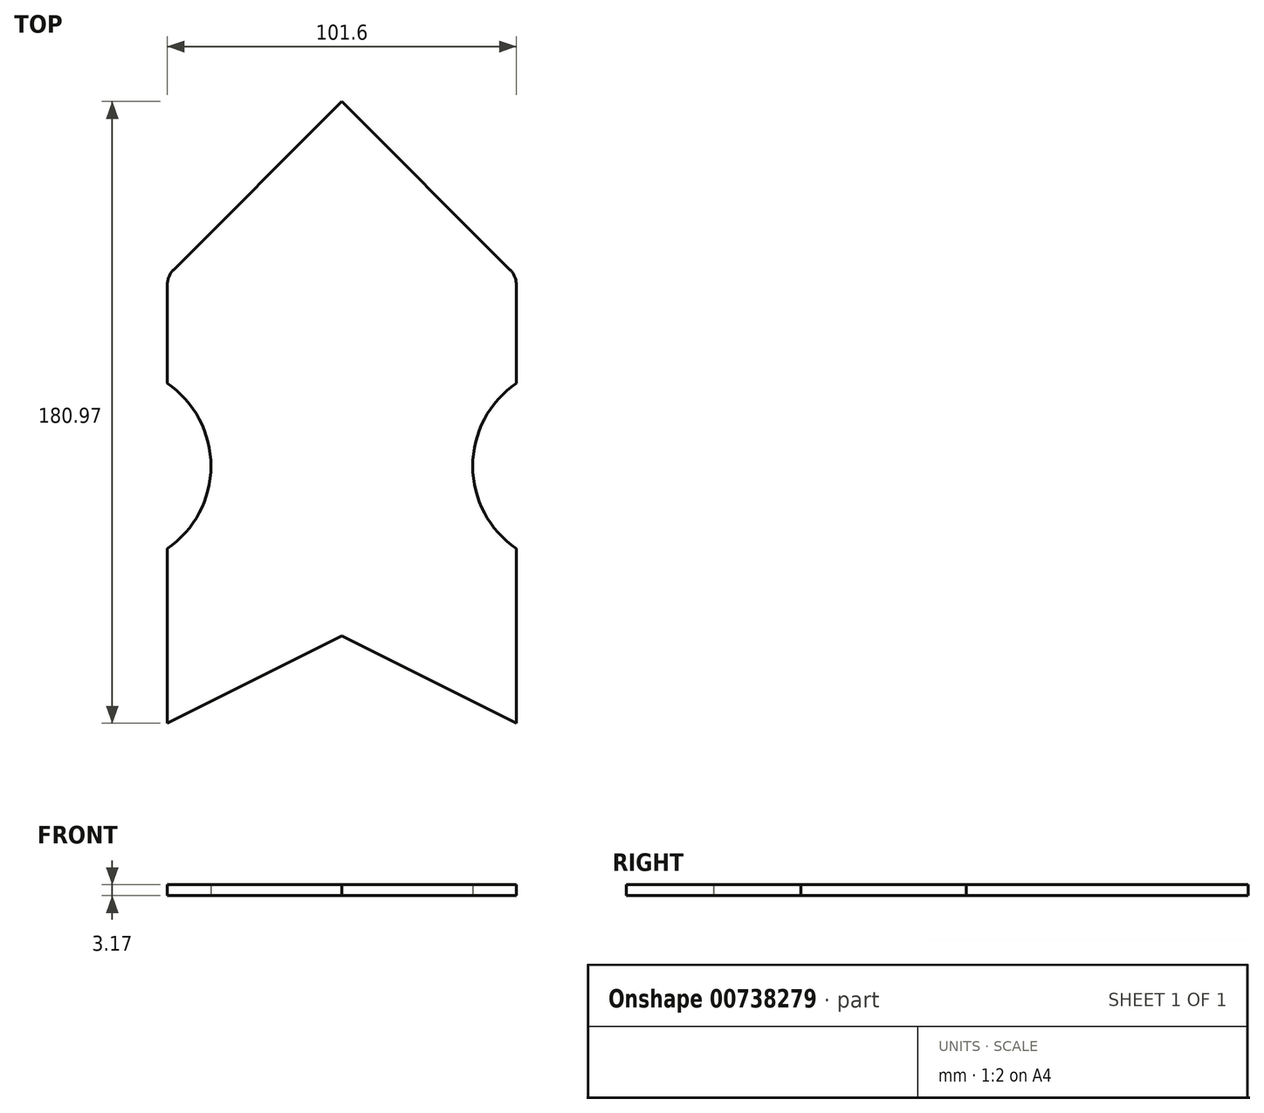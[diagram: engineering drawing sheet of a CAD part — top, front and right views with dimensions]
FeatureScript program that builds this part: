
annotation { "Feature Type Name" : "Feature", "Feature Type Description" : "" }
export const myFeature = defineFeature(function(context is Context, id is Id, definition is map)
    precondition{}
    {
        {
            var Q0;
            Q0=qCreatedBy(makeId("Top.planeOp"),FACE);
            var sketch = newSketch(context, id + "F0", { "sketchPlane" : qUnion([Q0])});
            skLineSegment(sketch, "E0", {"start": v(54.35, -30.5) * mm, "end": v(3.55, -5.1) * mm});
            skLineSegment(sketch, "E1", {"start": v(3.55, -5.1) * mm, "end": v(-47.25, -30.5) * mm});
            skLineSegment(sketch, "E2", {"start": v(-47.25, -30.5) * mm, "end": v(-47.25, 20.3) * mm});
            skLineSegment(sketch, "E3", {"start": v(54.35, -30.5) * mm, "end": v(54.35, 20.3) * mm});
            skLineSegment(sketch, "E4", {"start": v(54.35, 99.68) * mm, "end": v(-47.25, 99.68) * mm});
            skLineSegment(sketch, "E5", {"start": v(3.55, -5.1) * mm, "end": v(3.55, 150.48) * mm, "construction": true});
            skLineSegment(sketch, "E6", {"start": v(3.55, 150.48) * mm, "end": v(-45.39, 101.54) * mm});
            skLineSegment(sketch, "E7", {"start": v(52.5, 101.54) * mm, "end": v(3.55, 150.48) * mm});
            skLineSegment(sketch, "E8", {"start": v(-47.25, -30.5) * mm, "end": v(54.35, -30.5) * mm, "construction": true});
            skPoint(sketch, "E9.visualSharp", {"position": v(-47.25, 99.68) * mm});
            skArc(sketch, "E9.filletArc", {"start": v(-45.39, 101.54) * mm, "mid": v(-46.76, 99.48) * mm, "end": v(-47.25, 97.05) * mm});
            skPoint(sketch, "E10.visualSharp", {"position": v(54.35, 99.68) * mm});
            skArc(sketch, "E10.filletArc", {"start": v(54.35, 97.05) * mm, "mid": v(53.87, 99.48) * mm, "end": v(52.5, 101.54) * mm});
            skPoint(sketch, "E11", {"position": v(-47.25, 68.48) * mm});
            skPoint(sketch, "E12", {"position": v(-47.25, 20.3) * mm});
            skArc(sketch, "E13", {"start": v(-47.25, 20.3) * mm, "mid": v(-34.55, 44.4) * mm, "end": v(-47.25, 68.48) * mm});
            skPoint(sketch, "E14", {"position": v(54.35, 68.48) * mm});
            skPoint(sketch, "E15", {"position": v(54.35, 20.3) * mm});
            skArc(sketch, "E16", {"start": v(54.35, 68.48) * mm, "mid": v(41.65, 44.4) * mm, "end": v(54.35, 20.3) * mm});
            skLineSegment(sketch, "E17.trimOffspring", {"start": v(-47.25, 68.48) * mm, "end": v(-47.25, 97.05) * mm});
            skLineSegment(sketch, "E18.trimOffspring", {"start": v(54.35, 68.48) * mm, "end": v(54.35, 97.05) * mm});
            skLineSegment(sketch, "E19", {"start": v(-47.25, 68.48) * mm, "end": v(-47.25, 20.3) * mm, "construction": true});
            skLineSegment(sketch, "E20", {"start": v(54.35, 68.48) * mm, "end": v(54.35, 20.3) * mm, "construction": true});
            skLineSegment(sketch, "E21", {"start": v(-34.55, 44.4) * mm, "end": v(-47.25, 44.4) * mm, "construction": true});
            skLineSegment(sketch, "E22", {"start": v(41.65, 44.4) * mm, "end": v(54.35, 44.4) * mm, "construction": true});
            skSolve(sketch);
        }
        {
            var Q0;
            Q0 = qSketchRegion(id + "F0", true);
            extrude(context, id + "F1", {"entities" : qUnion([Q0]), "depth" : 3.17 * mm, "offsetDistance" : 25.4 * mm});
        }
    });
